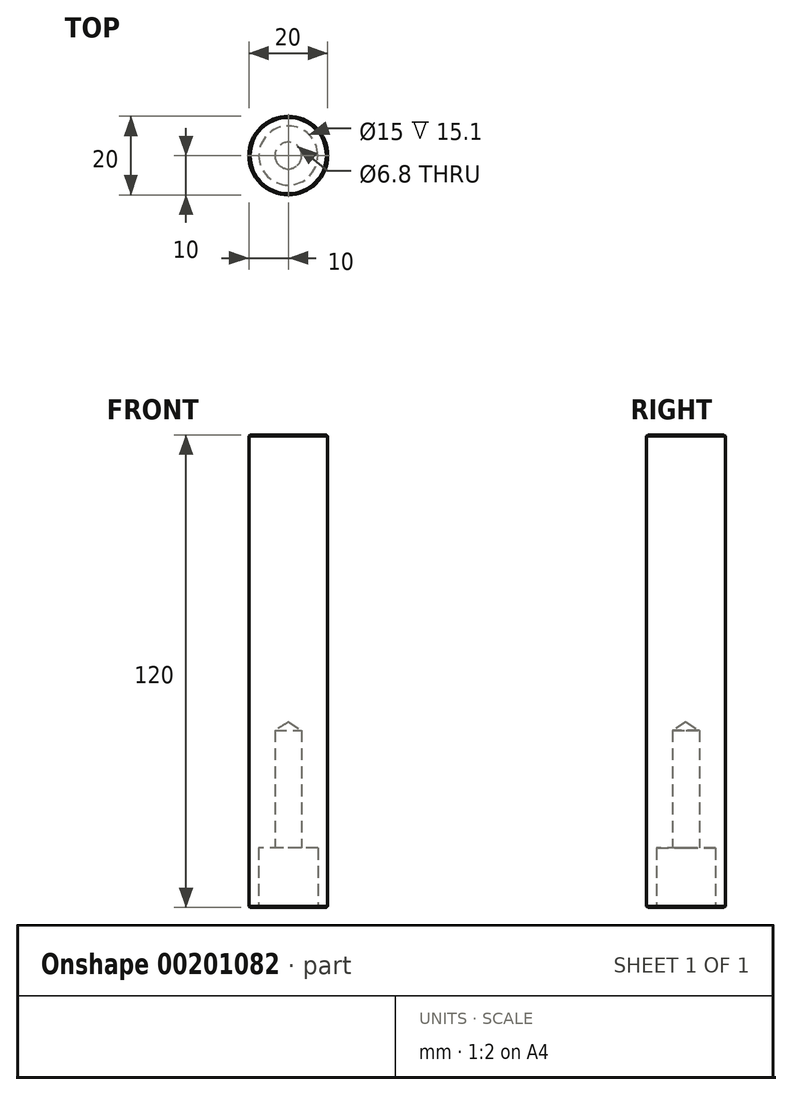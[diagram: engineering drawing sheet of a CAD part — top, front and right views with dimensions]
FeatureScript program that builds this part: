
annotation { "Feature Type Name" : "Feature", "Feature Type Description" : "" }
export const myFeature = defineFeature(function(context is Context, id is Id, definition is map)
    precondition{}
    {
        {
            var Q0;
            Q0=qCreatedBy(makeId("Top.planeOp"),FACE);
            var sketch = newSketch(context, id + "F0", { "sketchPlane" : qUnion([Q0])});
            skCircle(sketch, "E0", {"center": v(0, 0) * mm, "radius": 10 * mm});
            skCircle(sketch, "E1", {"center": v(0, 0) * mm, "radius": 7.5 * mm});
            skSolve(sketch);
        }
        {
            var Q0;
            Q0=makeQuery(id+"F0.imprint","IMPRINT",FACE,{"disambiguationData":[TD([[makeQuery(id+"F0.imprint","IMPRINT",EDGE,{"derivedFrom":sQuery(id+"F0.wireOp",EDGE,"E1")}),1.0]])]});
            var Q1;
            Q1=makeQuery(id+"F0.imprint","IMPRINT",FACE,{"disambiguationData":[TD([[makeQuery(id+"F0.imprint","IMPRINT",EDGE,{"derivedFrom":sQuery(id+"F0.wireOp",EDGE,"E0")}),1.0]])]});
            extrude(context, id + "F1", {"entities" : qUnion([Q0, Q1]), "depth" : 120 * mm});
        }
        {
            var Q0;
            Q0=makeQuery(id+"F0.imprint","IMPRINT",FACE,{"disambiguationData":[TD([[makeQuery(id+"F0.imprint","IMPRINT",EDGE,{"derivedFrom":sQuery(id+"F0.wireOp",EDGE,"E1")}),1.0]])]});
            extrude(context, id + "F2", {"entities" : qUnion([Q0]), "operationType" : NewBodyOperationType.REMOVE, "depth" : 15.1 * mm});
        }
        {
            var Q0;
            Q0=sQuery(id+"F0.wireOp",VERTEX,"E0.center");
            var Q1;
            Q1=makeQuery(id+"F1.opExtrude","SWEPT_BODY",BODY,{"disambiguationData":[OSD([sQuery(id+"F0.wireOp",EDGE,"E0")])]});
            hole(context, id + "F3", {"style" : HoleStyle.SIMPLE, "endStyle" : HoleEndStyle.BLIND, "oppositeDirection" : true, "standardTappedOrClearance" : lookupTablePath({ "standard" : "ISO", "engagement" : "75%", "pitch" : "1.25 mm", "size" : "M8", "type" : "Tapped" }), "standardBlindInLast" : lookupTablePath({ "standard" : "ISO", "engagement" : "75%", "pitch" : "1.25 mm", "size" : "M8", "type" : "Tapped" }), "holeDiameter" : 6.8 * mm, "holeDepth" : 45 * mm, "startFromSketch" : true, "locations" : qUnion([Q0]), "scope" : qUnion([Q1]), "majorDiameter" : 8 * mm});
        }
        {
            var Q0;
            Q0=makeQuery(id+"F1.opExtrude","CAP_EDGE",EDGE,{"disambiguationData":[OSD([sQuery(id+"F0.wireOp",EDGE,"E0")])],"isStart":false});
            var Q1;
            Q1=makeQuery(id+"F2.boolean.opBoolean","COPY",EDGE,{"derivedFrom":makeQuery(id+"F2.opExtrude","CAP_EDGE",EDGE,{"disambiguationData":[OSD([sQuery(id+"F0.wireOp",EDGE,"E1")])],"isStart":true})});
            var Q2;
            Q2=makeQuery(id+"F1.opExtrude","CAP_EDGE",EDGE,{"disambiguationData":[OSD([sQuery(id+"F0.wireOp",EDGE,"E0")])],"isStart":true});
            chamfer(context, id + "F4", {"entities" : qUnion([Q0, Q1, Q2]), "width" : 0.3 * mm, "tangentPropagation" : true});
        }
    });
